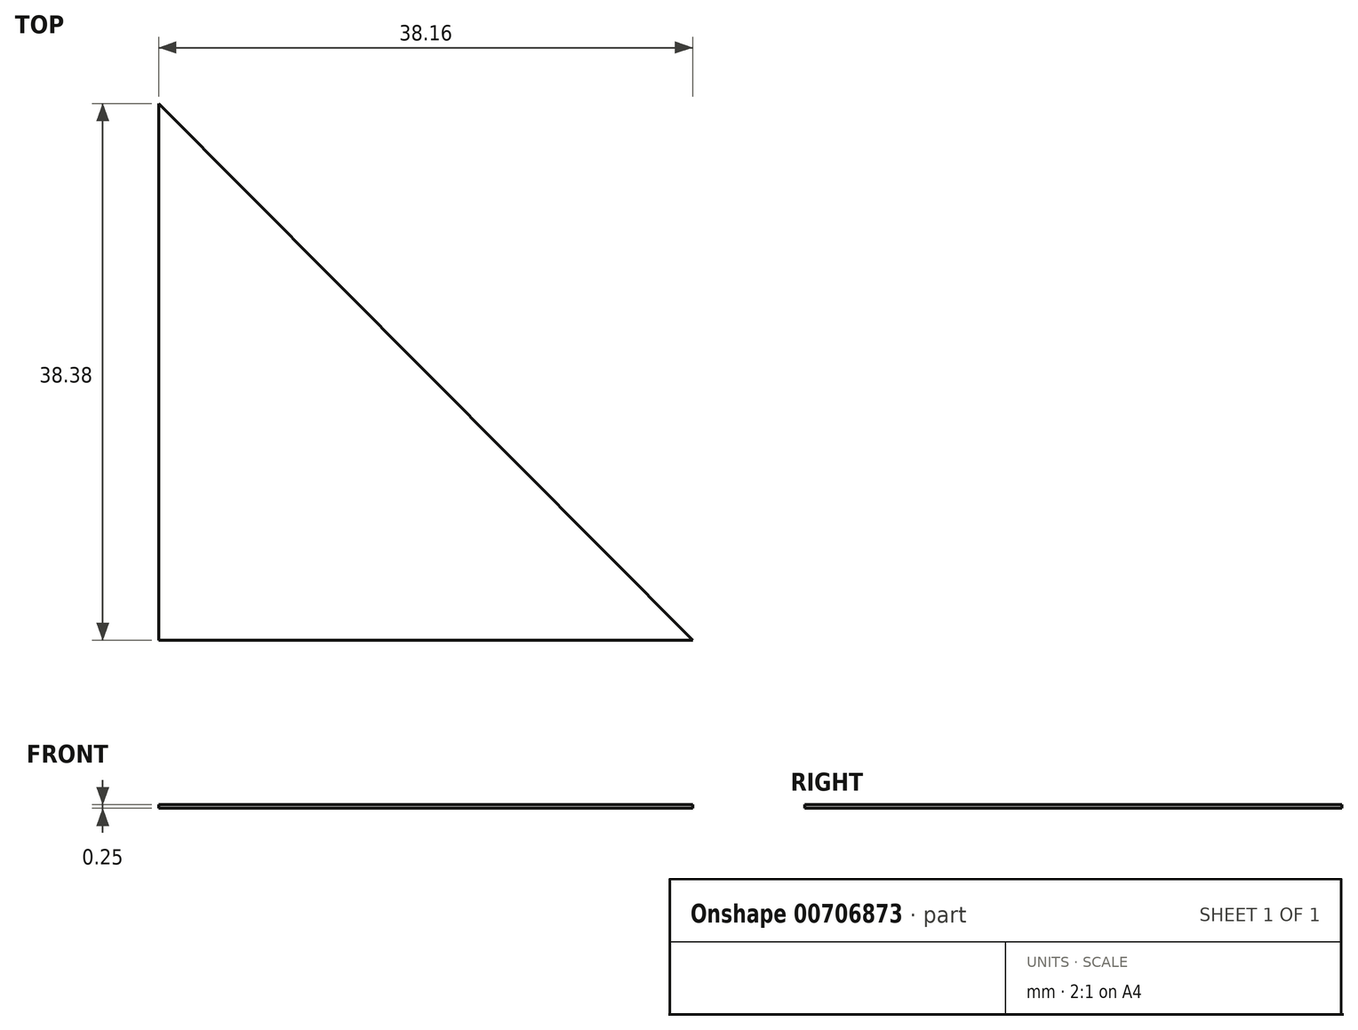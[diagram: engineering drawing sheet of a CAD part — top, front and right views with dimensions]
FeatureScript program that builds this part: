
annotation { "Feature Type Name" : "Feature", "Feature Type Description" : "" }
export const myFeature = defineFeature(function(context is Context, id is Id, definition is map)
    precondition{}
    {
        {
            var Q0;
            Q0=qCreatedBy(makeId("Top.planeOp"),FACE);
            var sketch = newSketch(context, id + "F0", { "sketchPlane" : qUnion([Q0])});
            skLineSegment(sketch, "E0", {"start": v(-44.43, -8.78) * mm, "end": v(-82.6, -8.78) * mm});
            skLineSegment(sketch, "E1", {"start": v(-82.6, -8.78) * mm, "end": v(-82.6, 29.6) * mm});
            skLineSegment(sketch, "E2", {"start": v(-82.6, 29.6) * mm, "end": v(-44.43, -8.78) * mm});
            skSolve(sketch);
        }
        {
            var Q0;
            Q0 = qSketchRegion(id + "F0", true);
            extrude(context, id + "F1", {"entities" : qUnion([Q0]), "depth" : 0.25 * mm, "offsetDistance" : 25.4 * mm});
        }
    });
